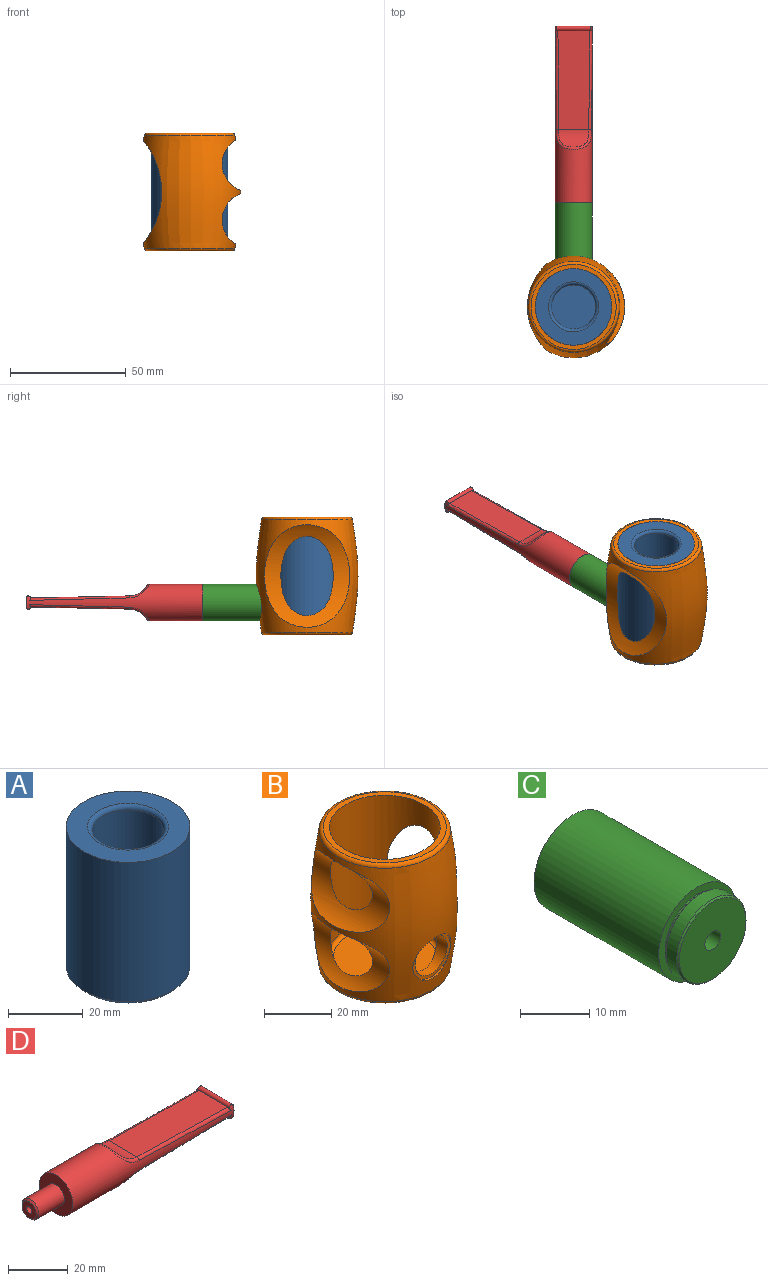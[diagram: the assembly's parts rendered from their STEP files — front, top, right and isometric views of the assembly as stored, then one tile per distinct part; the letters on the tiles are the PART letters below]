
ASSEMBLY  parts=4 mates=8
PART A: 8 faces, bbox 33x33x47 mm
  f0: cylinder r=16.51mm len=45.47mm, axis (0,0,1), area 4708.5mm2, adj f2,f6,f7
  f1: plane 29.97x29.97mm, normal (0,0,-1), area 705.5mm2, adj f6
  f2: plane 33.02x33.02mm, normal (0,0,1), area 490.2mm2, adj f0,f5
  f3: cylinder r=9.53mm len=39.37mm, axis (0,0,1), area 2348.2mm2, adj f4,f5,f7
  f4: plane 19.05x19.05mm, normal (0,0,1), area 285mm2, adj f3
  f5: torus R=10.79mm, axis (0,0,1), area 125.2mm2, adj f2,f3
  f6: cone r=16.51mm half-angle=45deg, axis (0,0,1), area 213.3mm2, adj f0,f1
  f7: cylinder r=1.59mm len=7.12mm, axis (0,-1,0), area 70mm2, adj f0,f3
PART B: 16 faces, bbox 43.9x43.9x50.8 mm
  f0: cylinder r=16.51mm len=45.72mm, axis (0,0,1), area 3493.2mm2, adj f2,f7,f8,f9,f12,f15
  f1: revolved ~48.64x43.92mm, area -6207.4mm2, adj f3,f7,f8,f9,f10
  f2: plane 36.67x36.67mm, normal (0,0,1), area 200mm2, adj f0,f3
  f3: torus R=18.34mm, axis (0,0,1), area 216.7mm2, adj f1,f2
  f4: torus R=18.34mm, axis (0,0,1), area 216.7mm2, adj f5
  f5: plane 36.67x36.67mm, normal (0,0,-1), area 970.8mm2, adj f4,f14
  f6: plane 30.48x30.48mm, normal (0,0,1), area 709.2mm2, adj f13,f15
  f7: cylinder r=12.06mm len=32.28mm, axis (0,-1,0), area 473.5mm2, adj f0,f1
  f8: cylinder r=34.92mm len=44.15mm, axis (0,-1,0), area 743.8mm2, adj f0,f1
  f9: cylinder r=12.06mm len=32.28mm, axis (0,-1,0), area 473.3mm2, adj f0,f1
  f10: cylinder r=7.94mm len=15.88mm, axis (0,1,0), area 44.5mm2, adj f1,f11
  f11: plane 15.88x15.88mm, normal (0,-1,0), area 55.6mm2, adj f10,f12
  f12: cylinder r=6.73mm len=13.46mm, axis (0,-1,0), area 158.9mm2, adj f0,f11
  f13: cylinder r=2.55mm len=5.11mm, axis (0,0,-1), area 11.9mm2, adj f6,f14
  f14: cone r=2.55mm half-angle=41deg, axis (0,0,-1), area 99.3mm2, adj f5,f13
  f15: torus R=15.24mm, axis (0,0,1), area 201.2mm2, adj f0,f6
PART C: 13 faces, bbox 15.9x28.4x15.9 mm
  f0: cylinder r=1.59mm len=7.97mm, axis (0,-1,0), area 79.5mm2, adj f4,f9
  f1: cylinder r=7.94mm len=25.4mm, axis (0,-1,0), area 1266.8mm2, adj f2,f3
  f2: plane 15.88x15.88mm, normal (0,1,0), area 126.7mm2, adj f1,f6
  f3: plane 15.88x15.88mm, normal (0,-1,0), area 58.8mm2, adj f1,f7
  f4: cone r=0mm half-angle=59deg, axis (0,1,0), area 48.5mm2, adj f0,f5
  f5: cylinder r=3.97mm len=17.68mm, axis (0,1,0), area 440.8mm2, adj f4,f6
  f6: cone r=3.97mm half-angle=30deg, axis (0,1,0), area 43.5mm2, adj f2,f5
  f7: cylinder r=6.65mm len=13.31mm, axis (0,1,0), area 15.9mm2, adj f3,f10
  f8: cylinder r=7.05mm len=14.1mm, axis (0,1,0), area 95.6mm2, adj f11,f12
  f9: plane 13.59x13.59mm, normal (0,-1,0), area 137.1mm2, adj f0,f12
  f10: plane 13.59x13.59mm, normal (0,1,0), area 5.9mm2, adj f7,f11
  f11: cone r=7.05mm half-angle=45deg, axis (0,-1,0), area 15.6mm2, adj f8,f10
  f12: cone r=6.79mm half-angle=45deg, axis (0,1,0), area 15.6mm2, adj f8,f9
PART D: 28 faces, bbox 89x17.3x16 mm
  f0: cylinder r=1.27mm len=38.1mm, axis (-1,0,0), area 304mm2, adj f6,f22,f25
  f1: cylinder r=7.94mm len=75.82mm, axis (-1,0,0), area 1556.8mm2, adj f2,f4,f10,f13,f14,f15,f16,f17
  f2: cylinder r=7.94mm len=1.27mm, axis (-1,0,0), area 0.2mm2, adj f1,f13
  f3: plane 15.11x3.81mm, normal (1,0,0), area 24.5mm2, adj f10,f13,f20,f21,f23,f24,f26,f27
  f4: plane 15.88x15.88mm, normal (-1,0,0), area 148.4mm2, adj f1,f5
  f5: cylinder r=3.97mm len=12.07mm, axis (1,0,0), area 300.9mm2, adj f4,f7
  f6: plane 6.67x6.67mm, normal (-1,0,0), area 29.8mm2, adj f0,f7
  f7: cone r=3.33mm half-angle=45deg, axis (1,0,0), area 20.6mm2, adj f5,f6
  f8: plane 42.76x13.63mm, normal (0.02,0,-1), area 568.9mm2, adj f9,f10,f17,f19
  f9: cylinder r=8.89mm len=13.16mm, axis (0,-1,0), area 100.3mm2, adj f8,f18
  f10: cylinder r=1.02mm len=15.77mm, axis (0,-1,0), area 46.9mm2, adj f1,f3,f8,f17,f19,f26,f27
  f11: cylinder r=8.89mm len=13.16mm, axis (0,-1,0), area 100.3mm2, adj f12,f15
  f12: plane 42.76x13.63mm, normal (0.02,0,1), area 568.9mm2, adj f11,f13,f14,f16
  f13: cylinder r=1.02mm len=15.77mm, axis (0,-1,0), area 46.6mm2, adj f1,f2,f3,f12,f14,f16,f26,f27
  f14: bspline ~43.24x1.92mm, area 68mm2, adj f1,f12,f13,f15
  f15: bspline ~15.37x9.68mm, area 36.2mm2, adj f1,f11,f14,f16
  f16: bspline ~43.24x1.92mm, area 68mm2, adj f1,f12,f13,f15
  f17: bspline ~43.24x1.92mm, area 68mm2, adj f1,f8,f10,f18
  f18: bspline ~15.37x9.68mm, area 36.2mm2, adj f1,f9,f17,f19
  f19: bspline ~43.24x1.92mm, area 68mm2, adj f1,f8,f10,f18
  f20: plane 50.8x10.8mm, normal (0,0,1), area 548.4mm2, adj f3,f22,f23,f24,f25
  f21: plane 50.8x10.8mm, normal (0,0,-1), area 548.4mm2, adj f3,f22,f23,f24,f25
  f22: plane 6.67x2.54mm, normal (1,0,0), area 13.7mm2, adj f0,f20,f21,f24
  f23: cylinder r=1.27mm len=50.8mm, axis (1,0,0), area 202.7mm2, adj f3,f20,f21,f25
  f24: cylinder r=1.27mm len=50.8mm, axis (1,0,0), area 202.7mm2, adj f3,f20,f21,f22
  f25: plane 6.67x2.54mm, normal (1,0,0), area 13.7mm2, adj f0,f20,f21,f23
  f26: torus R=7.56mm, axis (1,0,0), area 2.8mm2, adj f1,f3,f10,f13
  f27: torus R=7.56mm, axis (1,0,0), area 2.8mm2, adj f1,f3,f10,f13
PLACE A rot(axis=(0,1,0),0deg) t=(0,0,0)mm
PLACE B rot(axis=(0,0,1),180deg) t=(0,0,-25.4)mm
PLACE C rot(axis=(0,-1,0),33.2deg) t=(0,19.56,-36.83)mm
PLACE D rot(axis=(0,0,1),90deg) t=(0,44.96,-36.83)mm
MATE parallel A.f7 <-> C.f1  axis (0,-1,0) through (0,9.35,-36.83)mm
MATE cylindrical C.f1 <-> B.f10  axis (0,-1,0) through (0,44.96,-36.83)mm
MATE cylindrical A.f0 <-> B.f15  axis (0,0,1) through (0,0,0)mm
MATE parallel D.f20 <-> B.f14  axis (0,0,1) through (0,121.16,-38.1)mm
MATE planar C.f1 <-> D.f1  axis (0,1,0) through (0,44.96,-36.83)mm
MATE planar C.f1 <-> B.f10  axis (0,-1,0) through (0,19.56,-36.83)mm
MATE planar A.f0 <-> B.f3  axis (0,0,-1) through (0,0,-46.99)mm
MATE cylindrical D.f5 <-> C.f4  axis (0,1,0) through (0,38.93,-36.83)mm
